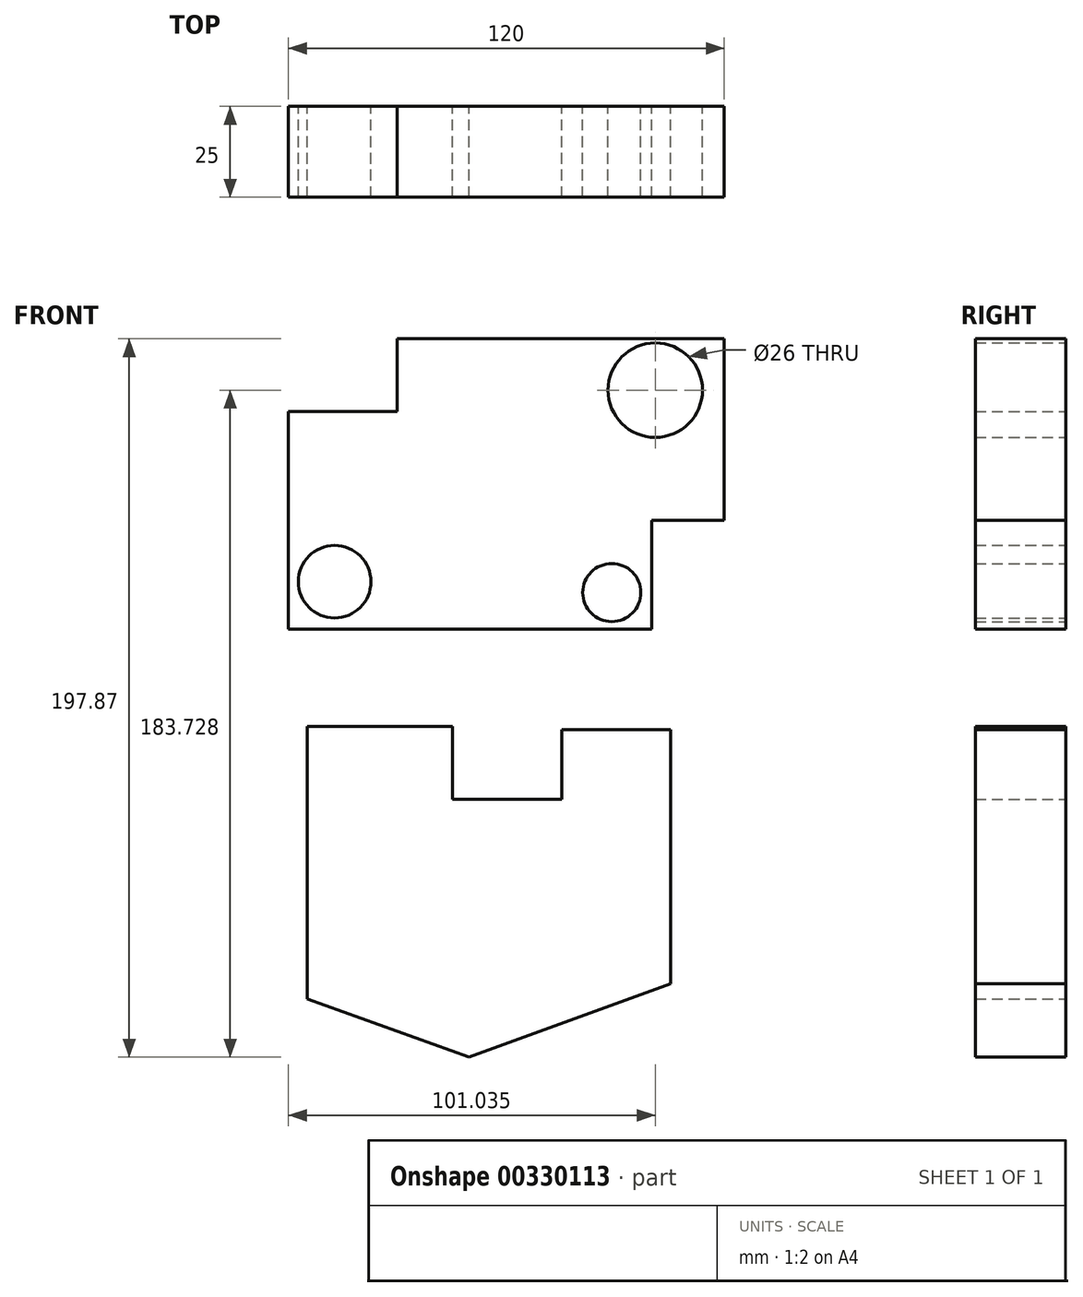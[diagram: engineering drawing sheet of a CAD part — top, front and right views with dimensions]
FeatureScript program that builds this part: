
annotation { "Feature Type Name" : "Feature", "Feature Type Description" : "" }
export const myFeature = defineFeature(function(context is Context, id is Id, definition is map)
    precondition{}
    {
        {
            var Q0;
            Q0=qCreatedBy(makeId("Front.planeOp"),FACE);
            var sketch = newSketch(context, id + "F0", { "sketchPlane" : qUnion([Q0])});
            skLineSegment(sketch, "E0", {"start": v(33.3, 27.7) * mm, "end": v(33.3, 87.7) * mm});
            skLineSegment(sketch, "E1", {"start": v(33.3, 87.7) * mm, "end": v(63.3, 87.7) * mm});
            skLineSegment(sketch, "E2", {"start": v(63.3, 87.7) * mm, "end": v(63.3, 107.7) * mm});
            skLineSegment(sketch, "E3", {"start": v(63.3, 107.7) * mm, "end": v(153.3, 107.7) * mm});
            skLineSegment(sketch, "E4", {"start": v(153.3, 107.7) * mm, "end": v(153.3, 57.7) * mm});
            skLineSegment(sketch, "E5", {"start": v(153.3, 57.7) * mm, "end": v(133.3, 57.7) * mm});
            skLineSegment(sketch, "E6", {"start": v(133.3, 57.7) * mm, "end": v(133.3, 27.7) * mm});
            skLineSegment(sketch, "E7", {"start": v(133.3, 27.7) * mm, "end": v(33.3, 27.7) * mm});
            skCircle(sketch, "E8", {"center": v(46.03, 40.79) * mm, "radius": 10 * mm});
            skCircle(sketch, "E9", {"center": v(134.34, 93.55) * mm, "radius": 13 * mm});
            skCircle(sketch, "E10", {"center": v(122.36, 37.8) * mm, "radius": 8 * mm});
            skLineSegment(sketch, "E11", {"start": v(38.54, -74.1) * mm, "end": v(38.54, 0.9) * mm});
            skLineSegment(sketch, "E12", {"start": v(38.54, 0.9) * mm, "end": v(78.54, 0.9) * mm});
            skLineSegment(sketch, "E13", {"start": v(78.54, 0.9) * mm, "end": v(78.54, -19.1) * mm});
            skLineSegment(sketch, "E14", {"start": v(78.54, -19.1) * mm, "end": v(108.54, -19.1) * mm});
            skLineSegment(sketch, "E15", {"start": v(108.54, -19.1) * mm, "end": v(108.54, 0) * mm});
            skLineSegment(sketch, "E16", {"start": v(108.54, 0) * mm, "end": v(138.54, 0) * mm});
            skLineSegment(sketch, "E17", {"start": v(138.54, 0) * mm, "end": v(138.54, -70) * mm});
            skLineSegment(sketch, "E18", {"start": v(138.54, -70) * mm, "end": v(83.1, -90.18) * mm});
            skLineSegment(sketch, "E19", {"start": v(38.54, -74.1) * mm, "end": v(83.1, -90.18) * mm});
            skSolve(sketch);
        }
        {
            var Q0;
            Q0=makeQuery(id+"F0.imprint","IMPRINT",FACE,{"disambiguationData":[TD([[makeQuery(id+"F0.imprint","IMPRINT",EDGE,{"derivedFrom":sQuery(id+"F0.wireOp",EDGE,"E0")}),-1.0]])]});
            var Q1;
            Q1=makeQuery(id+"F0.imprint","IMPRINT",FACE,{"disambiguationData":[TD([[makeQuery(id+"F0.imprint","IMPRINT",EDGE,{"derivedFrom":sQuery(id+"F0.wireOp",EDGE,"E11")}),-1.0]])]});
            extrude(context, id + "F1", {"entities" : qUnion([Q0, Q1]), "depth" : 25 * mm});
        }
    });
